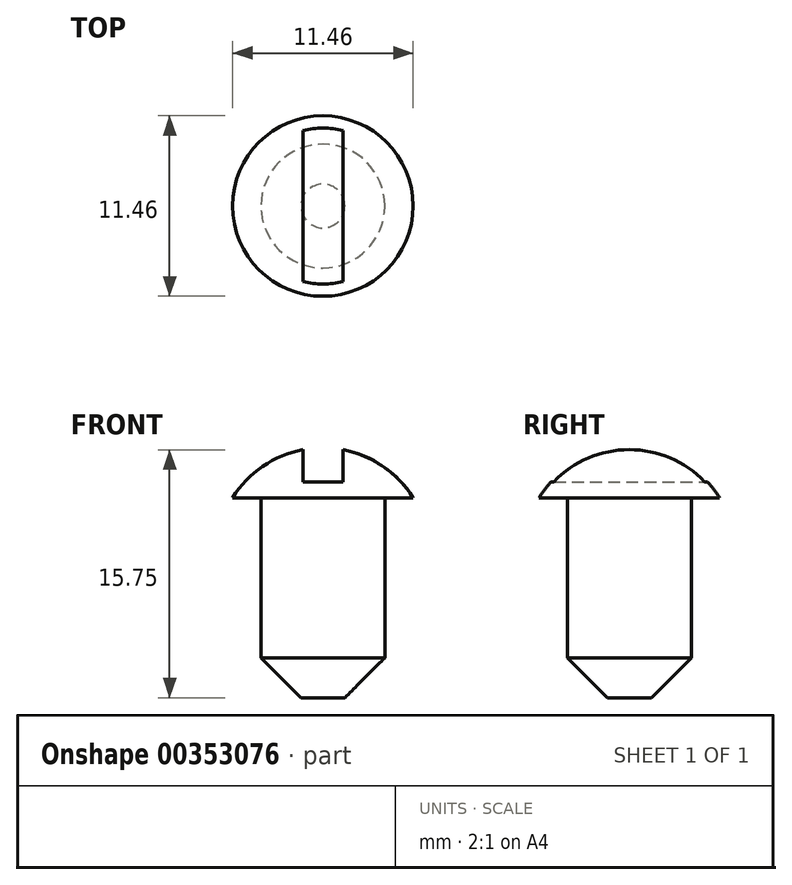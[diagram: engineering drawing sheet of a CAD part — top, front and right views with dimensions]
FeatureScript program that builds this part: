
annotation { "Feature Type Name" : "Feature", "Feature Type Description" : "" }
export const myFeature = defineFeature(function(context is Context, id is Id, definition is map)
    precondition{}
    {
        {
            var Q0;
            Q0=qCreatedBy(makeId("Front.planeOp"),FACE);
            var sketch = newSketch(context, id + "F0", { "sketchPlane" : qUnion([Q0])});
            skLineSegment(sketch, "E0", {"start": v(0, 0) * mm, "end": v(0, 9.11) * mm});
            skLineSegment(sketch, "E1", {"start": v(0, 0) * mm, "end": v(3.93, 0) * mm});
            skLineSegment(sketch, "E2", {"start": v(3.93, 0) * mm, "end": v(3.93, 12.7) * mm});
            skLineSegment(sketch, "E3", {"start": v(3.93, 12.7) * mm, "end": v(5.73, 12.7) * mm});
            skArc(sketch, "E4", {"start": v(5.73, 12.7) * mm, "mid": v(3.28, 15.03) * mm, "end": v(0, 15.88) * mm});
            skLineSegment(sketch, "E5", {"start": v(0, 9.11) * mm, "end": v(0, 15.88) * mm});
            skLineSegment(sketch, "E6", {"start": v(0, 0) * mm, "end": v(0, -6.26) * mm, "construction": true});
            skSolve(sketch);
        }
        {
            var Q0;
            Q0=makeQuery(id+"F0.imprint","IMPRINT",FACE,{"disambiguationData":[TD([[makeQuery(id+"F0.imprint","IMPRINT",EDGE,{"derivedFrom":sQuery(id+"F0.wireOp",EDGE,"E0")}),-1.0]])]});
            var Q1;
            Q1=sQuery(id+"F0.wireOp",EDGE,"E6");
            revolve(context, id + "F1", {"entities" : qUnion([Q0]), "axis" : qUnion([Q1]), "revolveType" : RevolveType.FULL});
        }
        {
            var Q0;
            Q0=qCreatedBy(makeId("Top.planeOp"),FACE);
            cPlane(context, id + "F2", {"entities" : qUnion([Q0]), "cplaneType" : CPlaneType.OFFSET, "offset" : 13.72 * mm, "width" : 152.4 * mm, "height" : 152.4 * mm});
        }
        {
            var Q0;
            Q0=qCreatedBy(id+"F2.planeOp",FACE);
            var sketch = newSketch(context, id + "F3", { "sketchPlane" : qUnion([Q0])});
            skLineSegment(sketch, "E7.bottom", {"start": v(-1.27, -5.08) * mm, "end": v(1.27, -5.08) * mm});
            skLineSegment(sketch, "E7.top", {"start": v(-1.27, 5.08) * mm, "end": v(1.27, 5.08) * mm});
            skLineSegment(sketch, "E7.left", {"start": v(-1.27, -5.08) * mm, "end": v(-1.27, 5.08) * mm});
            skLineSegment(sketch, "E7.right", {"start": v(1.27, -5.08) * mm, "end": v(1.27, 5.08) * mm});
            skPoint(sketch, "E7.middle", {"position": v(0, 0) * mm});
            skSolve(sketch);
        }
        {
            var Q0;
            Q0=makeQuery(id+"F3.imprint","IMPRINT",FACE,{"disambiguationData":[TD([[makeQuery(id+"F3.imprint","IMPRINT",EDGE,{"derivedFrom":sQuery(id+"F3.wireOp",EDGE,"E7.bottom")}),1.0]])]});
            extrude(context, id + "F4", {"entities" : qUnion([Q0]), "operationType" : NewBodyOperationType.REMOVE, "depth" : 25.4 * mm});
        }
        {
            var Q0;
            Q0=makeQuery(id+"F1.opRevolve","SWEPT_FACE",FACE,{"disambiguationData":[OSD([sQuery(id+"F0.wireOp",EDGE,"E1")])]});
            chamfer(context, id + "F5", {"entities" : qUnion([Q0]), "width" : 2.54 * mm, "tangentPropagation" : true});
        }
    });
